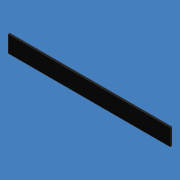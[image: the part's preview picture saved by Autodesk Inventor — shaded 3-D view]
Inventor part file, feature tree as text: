
AUTODESK INVENTOR PART (.ipt)
format: ipt  version: unknown  size: 167,424 bytes
history: native  units: mm (DEFAULTED — no unit token found)
features: extrude x1, sketch x1
ambient origin geometry x8: Origin, YZ Plane, XZ Plane, XY Plane, X Axis, Y Axis, Z Axis, Center Point
feature tree (2):
  extrude  "Extrusion1"  Depth=19.05mm
  sketch  "Sketch1"  dims[d0=184.15mm d1=19.05mm d2=1.905mm d3=0.0mm]
